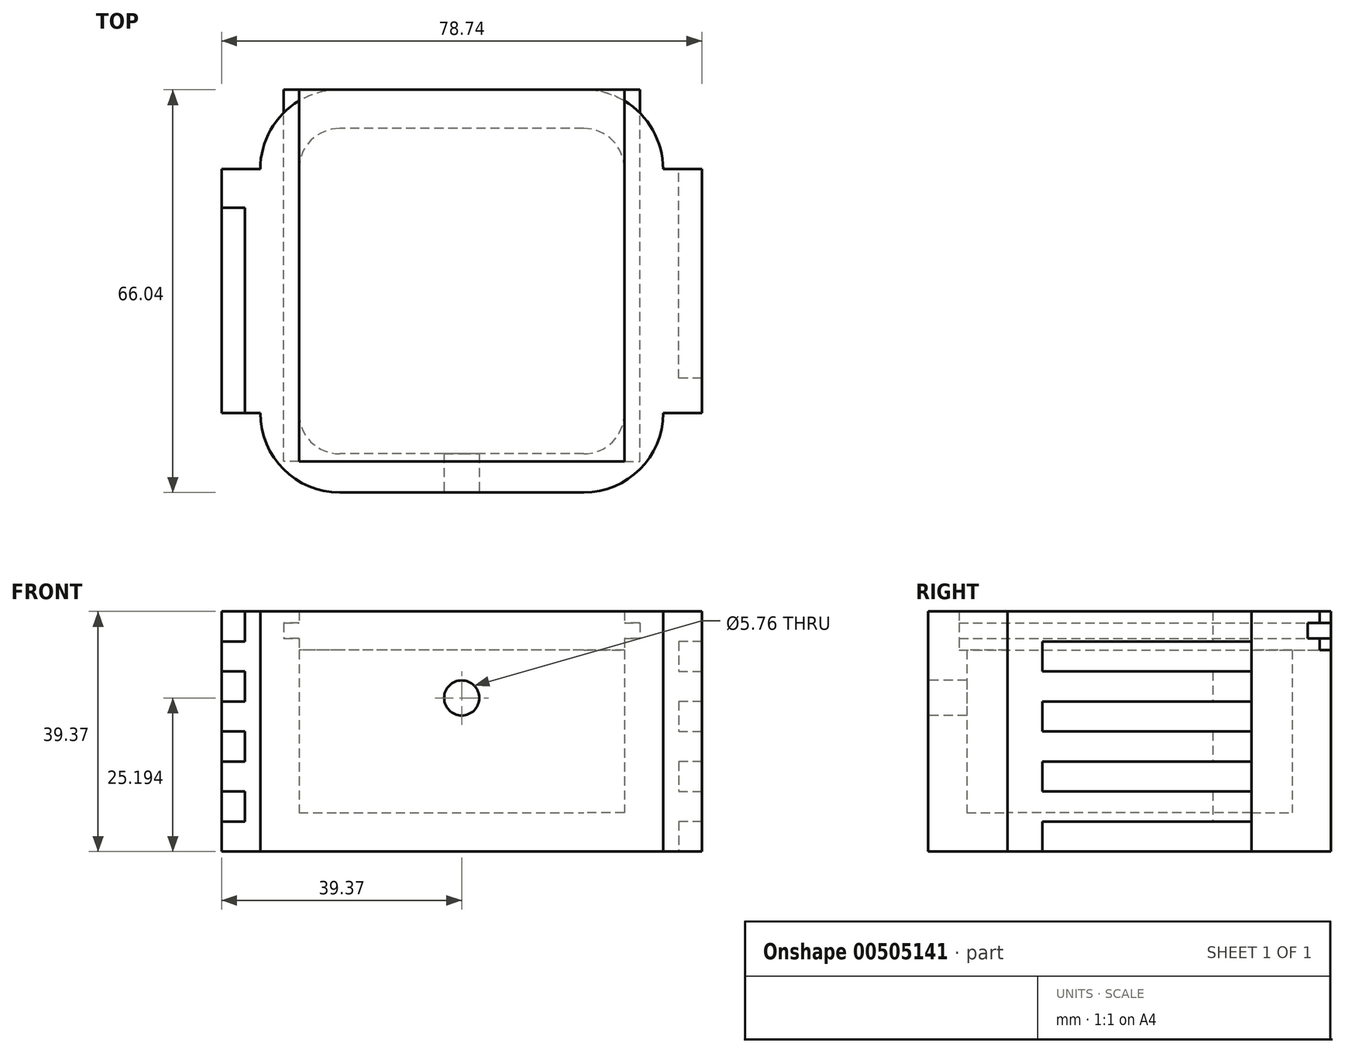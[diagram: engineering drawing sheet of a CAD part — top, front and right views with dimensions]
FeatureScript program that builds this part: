
annotation { "Feature Type Name" : "Feature", "Feature Type Description" : "" }
export const myFeature = defineFeature(function(context is Context, id is Id, definition is map)
    precondition{}
    {
        {
            var Q0;
            Q0=qCreatedBy(makeId("Top.planeOp"),FACE);
            var sketch = newSketch(context, id + "F0", { "sketchPlane" : qUnion([Q0])});
            skLineSegment(sketch, "E0", {"start": v(-20, 26.67) * mm, "end": v(20, 26.67) * mm});
            skLineSegment(sketch, "E1.MirrorCS", {"start": v(-20, -26.67) * mm, "end": v(20, -26.67) * mm});
            skLineSegment(sketch, "E2", {"start": v(-26.67, 20) * mm, "end": v(-26.67, -20) * mm});
            skLineSegment(sketch, "E3.MirrorCS", {"start": v(26.67, 20) * mm, "end": v(26.67, -20) * mm});
            skPoint(sketch, "E4.visualSharp", {"position": v(-26.67, 26.67) * mm});
            skArc(sketch, "E4.filletArc", {"start": v(-20, 26.67) * mm, "mid": v(-24.72, 24.72) * mm, "end": v(-26.67, 20) * mm});
            skPoint(sketch, "E5.visualSharp", {"position": v(26.67, 26.67) * mm});
            skArc(sketch, "E5.filletArc", {"start": v(26.67, 20) * mm, "mid": v(24.72, 24.72) * mm, "end": v(20, 26.67) * mm});
            skPoint(sketch, "E6.visualSharp", {"position": v(26.67, -26.67) * mm});
            skArc(sketch, "E6.filletArc", {"start": v(20, -26.67) * mm, "mid": v(24.72, -24.72) * mm, "end": v(26.67, -20) * mm});
            skPoint(sketch, "E7.visualSharp", {"position": v(-26.67, -26.67) * mm});
            skArc(sketch, "E7.filletArc", {"start": v(-26.67, -20) * mm, "mid": v(-24.72, -24.72) * mm, "end": v(-20, -26.67) * mm});
            skPoint(sketch, "E8", {"position": v(0, 33.02) * mm});
            skLineSegment(sketch, "E9", {"start": v(-20, 33.02) * mm, "end": v(20, 33.02) * mm});
            skLineSegment(sketch, "E10.MirrorCS", {"start": v(-20, -33.02) * mm, "end": v(20, -33.02) * mm});
            skPoint(sketch, "E11", {"position": v(33.02, 0) * mm});
            skPoint(sketch, "E11.positionSnap0", {"position": v(26.67, 0) * mm});
            skLineSegment(sketch, "E12", {"start": v(33.02, 20) * mm, "end": v(33.02, -20) * mm});
            skLineSegment(sketch, "E13.MirrorCS", {"start": v(-33.02, 20) * mm, "end": v(-33.02, -20) * mm});
            skArc(sketch, "E14", {"start": v(33.02, 20) * mm, "mid": v(29.2, 29.2) * mm, "end": v(20, 33.02) * mm});
            skArc(sketch, "E15.MirrorCS", {"start": v(-33.02, 20) * mm, "mid": v(-29.2, 29.2) * mm, "end": v(-20, 33.02) * mm});
            skArc(sketch, "E16.MirrorCS", {"start": v(-33.02, -20) * mm, "mid": v(-29.2, -29.2) * mm, "end": v(-20, -33.02) * mm});
            skArc(sketch, "E17.MirrorCS", {"start": v(33.02, -20) * mm, "mid": v(29.2, -29.2) * mm, "end": v(20, -33.02) * mm});
            skSolve(sketch);
        }
        {
            var Q0;
            Q0 = qSketchRegion(id + "F0", true);
            extrude(context, id + "F1", {"entities" : qUnion([Q0]), "depth" : 39.37 * mm});
        }
        {
            var Q0;
            Q0=makeQuery(id+"F0.imprint","IMPRINT",FACE,{"disambiguationData":[TD([[makeQuery(id+"F0.imprint","IMPRINT",EDGE,{"derivedFrom":sQuery(id+"F0.wireOp",EDGE,"E0")}),-1.0]])]});
            extrude(context, id + "F2", {"entities" : qUnion([Q0]), "operationType" : NewBodyOperationType.ADD, "depth" : 6.35 * mm});
        }
        {
            var Q0;
            Q0=makeQuery(id+"F1.opExtrude","SWEPT_FACE",FACE,{"disambiguationData":[OSD([sQuery(id+"F0.wireOp",EDGE,"E9")])]});
            var sketch = newSketch(context, id + "F3", { "sketchPlane" : qUnion([Q0])});
            skPoint(sketch, "E18", {"position": v(0, 39.37) * mm});
            skPoint(sketch, "E19", {"position": v(20, 29.99) * mm});
            skPoint(sketch, "E20", {"position": v(33, 29.99) * mm});
            skPoint(sketch, "E21.MirrorP", {"position": v(-20, 29.99) * mm});
            skPoint(sketch, "E22.MirrorP", {"position": v(-26.66, 29.99) * mm});
            skPoint(sketch, "E23.MirrorP", {"position": v(-33, 29.99) * mm});
            skLineSegment(sketch, "E24", {"start": v(0, 39.37) * mm, "end": v(26.67, 39.37) * mm});
            skLineSegment(sketch, "E25.MirrorCS", {"start": v(0, 39.37) * mm, "end": v(-26.67, 39.37) * mm});
            skPoint(sketch, "E26", {"position": v(0, 0) * mm});
            skPoint(sketch, "E27", {"position": v(0, 6.35) * mm});
            skPoint(sketch, "E28", {"position": v(-26.67, 33.02) * mm});
            skPoint(sketch, "E29", {"position": v(-26.67, 39.37) * mm});
            skPoint(sketch, "E30.MirrorP", {"position": v(26.67, 33.02) * mm});
            skLineSegment(sketch, "E31", {"start": v(-26.67, 33.02) * mm, "end": v(26.67, 33.02) * mm});
            skLineSegment(sketch, "E32", {"start": v(26.67, 39.37) * mm, "end": v(26.67, 33.02) * mm});
            skLineSegment(sketch, "E33", {"start": v(-26.67, 39.37) * mm, "end": v(-26.67, 33.02) * mm});
            skPoint(sketch, "E34", {"position": v(-26.67, 37.46) * mm});
            skPoint(sketch, "E35", {"position": v(-26.67, 34.92) * mm});
            skPoint(sketch, "E36", {"position": v(-29.2, 34.92) * mm});
            skPoint(sketch, "E37", {"position": v(-29.2, 37.46) * mm});
            skLineSegment(sketch, "E38", {"start": v(-26.67, 37.46) * mm, "end": v(-29.2, 37.46) * mm});
            skLineSegment(sketch, "E39", {"start": v(-29.2, 34.92) * mm, "end": v(-26.67, 34.92) * mm});
            skLineSegment(sketch, "E40.MirrorCS", {"start": v(26.67, 37.46) * mm, "end": v(29.2, 37.46) * mm});
            skLineSegment(sketch, "E41.MirrorCS", {"start": v(29.2, 34.92) * mm, "end": v(26.67, 34.92) * mm});
            skLineSegment(sketch, "E42", {"start": v(-29.2, 37.46) * mm, "end": v(-29.2, 34.92) * mm});
            skLineSegment(sketch, "E43.MirrorCS", {"start": v(29.2, 37.46) * mm, "end": v(29.2, 34.92) * mm});
            skSolve(sketch);
        }
        {
            var Q0;
            {var subQ0=sQuery(id+"F3.wireOp",EDGE,"E38");Q0=makeQuery(id+"F3.imprint","IMPRINT",FACE,{"disambiguationData":[TD([[makeQuery(id+"F3.imprint","IMPRINT",EDGE,{"derivedFrom":subQ0}),1.0]])]});}
            var Q1;
            {var subQ0=sQuery(id+"F3.wireOp",EDGE,"E40.MirrorCS");Q1=makeQuery(id+"F3.imprint","IMPRINT",FACE,{"disambiguationData":[TD([[makeQuery(id+"F3.imprint","IMPRINT",EDGE,{"derivedFrom":subQ0}),-1.0]])]});}
            var Q2;
            {var subQ0=sQuery(id+"F3.wireOp",EDGE,"E24");var subQ6=sQuery(id+"F3.wireOp",EDGE,"E25.MirrorCS");var subQ9=makeQuery(id+"F3.imprint","INTERSECT",VERTEX,{"derivedFrom":[subQ0,subQ6]});Q2=makeQuery(id+"F3.imprint","IMPRINT",FACE,{"disambiguationData":[TD([[makeQuery(id+"F3.imprint","IMPRINT",EDGE,{"disambiguationData":[TD([[subQ9,1.0]])],"derivedFrom":subQ0}),1.0]])]});}
            var Q3;
            {var subQ0=sQuery(id+"F3.wireOp",EDGE,"E33");var subQ3=sQuery(id+"F3.wireOp",EDGE,"E25.MirrorCS");var subQ4=makeQuery(id+"F3.imprint","INTERSECT",VERTEX,{"derivedFrom":[subQ3,subQ0]});Q3=makeQuery(id+"F3.imprint","IMPRINT",FACE,{"disambiguationData":[TD([[makeQuery(id+"F3.imprint","IMPRINT",EDGE,{"disambiguationData":[TD([[subQ4,-1.0]])],"derivedFrom":subQ0}),1.0]])]});}
            var Q4;
            {var subQ0=sQuery(id+"F3.wireOp",EDGE,"E32");var subQ3=sQuery(id+"F3.wireOp",EDGE,"E24");var subQ4=makeQuery(id+"F3.imprint","INTERSECT",VERTEX,{"derivedFrom":[subQ3,subQ0]});Q4=makeQuery(id+"F3.imprint","IMPRINT",FACE,{"disambiguationData":[TD([[makeQuery(id+"F3.imprint","IMPRINT",EDGE,{"disambiguationData":[TD([[subQ4,-1.0]])],"derivedFrom":subQ0}),-1.0]])]});}
            extrude(context, id + "F4", {"entities" : qUnion([Q0, Q1, Q2, Q3, Q4]), "operationType" : NewBodyOperationType.REMOVE, "oppositeDirection" : true, "depth" : 60.96 * mm});
        }
        {
            var Q0;
            {var subQ0=sQuery(id+"F3.wireOp",EDGE,"E40.MirrorCS");Q0=makeQuery(id+"F3.imprint","IMPRINT",FACE,{"disambiguationData":[TD([[makeQuery(id+"F3.imprint","IMPRINT",EDGE,{"derivedFrom":subQ0}),-1.0]])]});}
            var Q1;
            {var subQ0=sQuery(id+"F3.wireOp",EDGE,"E24");var subQ6=sQuery(id+"F3.wireOp",EDGE,"E25.MirrorCS");var subQ9=makeQuery(id+"F3.imprint","INTERSECT",VERTEX,{"derivedFrom":[subQ0,subQ6]});Q1=makeQuery(id+"F3.imprint","IMPRINT",FACE,{"disambiguationData":[TD([[makeQuery(id+"F3.imprint","IMPRINT",EDGE,{"disambiguationData":[TD([[subQ9,1.0]])],"derivedFrom":subQ0}),1.0]])]});}
            var Q2;
            {var subQ0=sQuery(id+"F3.wireOp",EDGE,"E32");var subQ3=sQuery(id+"F3.wireOp",EDGE,"E24");var subQ4=makeQuery(id+"F3.imprint","INTERSECT",VERTEX,{"derivedFrom":[subQ3,subQ0]});Q2=makeQuery(id+"F3.imprint","IMPRINT",FACE,{"disambiguationData":[TD([[makeQuery(id+"F3.imprint","IMPRINT",EDGE,{"disambiguationData":[TD([[subQ4,-1.0]])],"derivedFrom":subQ0}),-1.0]])]});}
            var Q3;
            {var subQ0=sQuery(id+"F3.wireOp",EDGE,"E33");var subQ3=sQuery(id+"F3.wireOp",EDGE,"E25.MirrorCS");var subQ4=makeQuery(id+"F3.imprint","INTERSECT",VERTEX,{"derivedFrom":[subQ3,subQ0]});Q3=makeQuery(id+"F3.imprint","IMPRINT",FACE,{"disambiguationData":[TD([[makeQuery(id+"F3.imprint","IMPRINT",EDGE,{"disambiguationData":[TD([[subQ4,-1.0]])],"derivedFrom":subQ0}),1.0]])]});}
            var Q4;
            {var subQ0=sQuery(id+"F3.wireOp",EDGE,"E38");Q4=makeQuery(id+"F3.imprint","IMPRINT",FACE,{"disambiguationData":[TD([[makeQuery(id+"F3.imprint","IMPRINT",EDGE,{"derivedFrom":subQ0}),1.0]])]});}
            extrude(context, id + "F5", {"entities" : qUnion([Q0, Q1, Q2, Q3, Q4]), "oppositeDirection" : true, "depth" : 60.96 * mm});
        }
        {
            var Q0;
            Q0=makeQuery(id+"F1.opExtrude","SWEPT_FACE",FACE,{"disambiguationData":[OSD([sQuery(id+"F0.wireOp",EDGE,"E12")])]});
            var sketch = newSketch(context, id + "F6", { "sketchPlane" : qUnion([Q0])});
            skLineSegment(sketch, "E44.bottom", {"start": v(20, 39.37) * mm, "end": v(-20, 39.37) * mm});
            skLineSegment(sketch, "E44.top", {"start": v(20, 0) * mm, "end": v(-20, 0) * mm});
            skLineSegment(sketch, "E44.left", {"start": v(20, 39.37) * mm, "end": v(20, 0) * mm});
            skLineSegment(sketch, "E44.right", {"start": v(-20, 39.37) * mm, "end": v(-20, 0) * mm});
            skSolve(sketch);
        }
        {
            var Q0;
            Q0 = qSketchRegion(id + "F6", true);
            extrude(context, id + "F7", {"entities" : qUnion([Q0]), "operationType" : NewBodyOperationType.ADD, "depth" : 6.35 * mm});
        }
        {
            var Q0;
            Q0=makeQuery(id+"F7.opExtrude","SWEPT_FACE",FACE,{"disambiguationData":[OSD([sQuery(id+"F6.wireOp",EDGE,"E44.left")])]});
            var sketch = newSketch(context, id + "F8", { "sketchPlane" : qUnion([Q0])});
            skPoint(sketch, "E45", {"position": v(-39.37, 19.69) * mm});
            skPoint(sketch, "E46", {"position": v(-39.37, 39.37) * mm});
            skPoint(sketch, "E47", {"position": v(-39.37, 0) * mm});
            skPoint(sketch, "E48", {"position": v(-39.37, 29.53) * mm});
            skPoint(sketch, "E49.MirrorP", {"position": v(-39.37, 9.84) * mm});
            skPoint(sketch, "E50", {"position": v(-39.37, 34.44) * mm});
            skPoint(sketch, "E51.MirrorP", {"position": v(-39.37, 24.61) * mm});
            skPoint(sketch, "E52.MirrorP", {"position": v(-39.37, 14.76) * mm});
            skPoint(sketch, "E53.MirrorP", {"position": v(-39.37, 4.93) * mm});
            skLineSegment(sketch, "E54", {"start": v(39.37, 4.93) * mm, "end": v(35.56, 4.93) * mm});
            skLineSegment(sketch, "E55", {"start": v(35.56, 4.93) * mm, "end": v(35.56, 9.84) * mm});
            skLineSegment(sketch, "E56", {"start": v(35.56, 9.84) * mm, "end": v(39.37, 9.84) * mm});
            skLineSegment(sketch, "E57", {"start": v(39.37, 14.76) * mm, "end": v(35.56, 14.76) * mm});
            skLineSegment(sketch, "E58", {"start": v(35.56, 14.76) * mm, "end": v(35.56, 19.68) * mm});
            skLineSegment(sketch, "E59", {"start": v(35.56, 19.68) * mm, "end": v(39.37, 19.68) * mm});
            skLineSegment(sketch, "E60", {"start": v(39.37, 24.61) * mm, "end": v(35.56, 24.61) * mm});
            skLineSegment(sketch, "E61", {"start": v(35.56, 24.61) * mm, "end": v(35.56, 29.53) * mm});
            skLineSegment(sketch, "E62", {"start": v(35.56, 29.53) * mm, "end": v(39.37, 29.53) * mm});
            skLineSegment(sketch, "E63", {"start": v(39.37, 34.44) * mm, "end": v(35.56, 34.44) * mm});
            skLineSegment(sketch, "E64", {"start": v(35.56, 34.44) * mm, "end": v(35.56, 39.37) * mm});
            skLineSegment(sketch, "E65", {"start": v(-35.56, 0) * mm, "end": v(-39.37, 0) * mm});
            skPoint(sketch, "E66", {"position": v(0, 20.46) * mm});
            skPoint(sketch, "E67", {"position": v(0, 39.45) * mm});
            skLineSegment(sketch, "E68", {"start": v(39.37, 0) * mm, "end": v(39.37, 4.93) * mm});
            skLineSegment(sketch, "E69", {"start": v(39.37, 0) * mm, "end": v(33.02, 0) * mm});
            skLineSegment(sketch, "E70", {"start": v(33.02, 0) * mm, "end": v(33.02, 39.37) * mm});
            skLineSegment(sketch, "E71", {"start": v(33.02, 39.37) * mm, "end": v(35.56, 39.37) * mm});
            skLineSegment(sketch, "E72", {"start": v(39.37, 14.76) * mm, "end": v(39.37, 9.84) * mm});
            skLineSegment(sketch, "E73", {"start": v(39.37, 34.44) * mm, "end": v(39.37, 29.53) * mm});
            skLineSegment(sketch, "E74", {"start": v(39.37, 24.61) * mm, "end": v(39.37, 19.68) * mm});
            skLineSegment(sketch, "E75", {"start": v(-39.37, 34.44) * mm, "end": v(-35.56, 34.44) * mm});
            skLineSegment(sketch, "E76", {"start": v(-35.56, 34.44) * mm, "end": v(-35.56, 29.53) * mm});
            skLineSegment(sketch, "E77", {"start": v(-35.56, 29.53) * mm, "end": v(-39.37, 29.53) * mm});
            skLineSegment(sketch, "E78", {"start": v(-39.37, 24.61) * mm, "end": v(-35.56, 24.61) * mm});
            skLineSegment(sketch, "E79", {"start": v(-35.56, 24.61) * mm, "end": v(-35.56, 19.69) * mm});
            skLineSegment(sketch, "E80", {"start": v(-35.56, 19.69) * mm, "end": v(-39.37, 19.69) * mm});
            skLineSegment(sketch, "E81", {"start": v(-39.37, 14.76) * mm, "end": v(-35.56, 14.76) * mm});
            skLineSegment(sketch, "E82", {"start": v(-35.56, 14.76) * mm, "end": v(-35.56, 9.84) * mm});
            skLineSegment(sketch, "E83", {"start": v(-35.56, 9.84) * mm, "end": v(-39.37, 9.84) * mm});
            skLineSegment(sketch, "E84", {"start": v(-39.37, 4.93) * mm, "end": v(-35.56, 4.93) * mm});
            skLineSegment(sketch, "E85", {"start": v(-35.56, 4.93) * mm, "end": v(-35.56, 0) * mm});
            skLineSegment(sketch, "E86", {"start": v(-39.37, 39.37) * mm, "end": v(-39.37, 34.44) * mm});
            skLineSegment(sketch, "E87", {"start": v(-39.37, 39.37) * mm, "end": v(-33.02, 39.37) * mm});
            skLineSegment(sketch, "E88", {"start": v(-33.02, 39.37) * mm, "end": v(-33.02, 0) * mm});
            skLineSegment(sketch, "E89", {"start": v(-33.02, 0) * mm, "end": v(-35.56, 0) * mm});
            skLineSegment(sketch, "E90", {"start": v(-39.37, 24.61) * mm, "end": v(-39.37, 29.53) * mm});
            skLineSegment(sketch, "E91", {"start": v(-39.37, 4.93) * mm, "end": v(-39.37, 9.84) * mm});
            skLineSegment(sketch, "E92", {"start": v(-39.37, 14.76) * mm, "end": v(-39.37, 19.69) * mm});
            skLineSegment(sketch, "E93", {"start": v(35.56, 39.37) * mm, "end": v(39.37, 39.37) * mm});
            skLineSegment(sketch, "E94", {"start": v(39.37, 39.37) * mm, "end": v(39.37, 34.44) * mm});
            skLineSegment(sketch, "E95", {"start": v(39.37, 29.53) * mm, "end": v(39.37, 24.61) * mm});
            skLineSegment(sketch, "E96", {"start": v(39.37, 19.68) * mm, "end": v(39.37, 14.76) * mm});
            skLineSegment(sketch, "E97", {"start": v(39.37, 9.84) * mm, "end": v(39.37, 4.93) * mm});
            skSolve(sketch);
        }
        {
            var Q0;
            Q0=makeQuery(id+"F1.opExtrude","SWEPT_FACE",FACE,{"disambiguationData":[OSD([sQuery(id+"F0.wireOp",EDGE,"E13.MirrorCS")])]});
            extrude(context, id + "F9", {"entities" : qUnion([Q0]), "operationType" : NewBodyOperationType.ADD, "depth" : 6.35 * mm});
        }
        {
            var Q0;
            {var subQ0=sQuery(id+"F8.wireOp",EDGE,"E75");Q0=makeQuery(id+"F8.imprint","IMPRINT",FACE,{"disambiguationData":[TD([[makeQuery(id+"F8.imprint","IMPRINT",EDGE,{"derivedFrom":subQ0}),-1.0]])]});}
            var Q1;
            {var subQ0=sQuery(id+"F8.wireOp",EDGE,"E78");Q1=makeQuery(id+"F8.imprint","IMPRINT",FACE,{"disambiguationData":[TD([[makeQuery(id+"F8.imprint","IMPRINT",EDGE,{"derivedFrom":subQ0}),-1.0]])]});}
            var Q2;
            {var subQ0=sQuery(id+"F8.wireOp",EDGE,"E81");Q2=makeQuery(id+"F8.imprint","IMPRINT",FACE,{"disambiguationData":[TD([[makeQuery(id+"F8.imprint","IMPRINT",EDGE,{"derivedFrom":subQ0}),-1.0]])]});}
            var Q3;
            {var subQ0=sQuery(id+"F8.wireOp",EDGE,"E65");Q3=makeQuery(id+"F8.imprint","IMPRINT",FACE,{"disambiguationData":[TD([[makeQuery(id+"F8.imprint","IMPRINT",EDGE,{"derivedFrom":subQ0}),1.0]])]});}
            extrude(context, id + "F10", {"entities" : qUnion([Q0, Q1, Q2, Q3]), "operationType" : NewBodyOperationType.REMOVE, "oppositeDirection" : true, "depth" : 34.3 * mm});
        }
        {
            var Q0;
            Q0=makeQuery(id+"F8.imprint","IMPRINT",FACE,{"disambiguationData":[TD([[makeQuery(id+"F8.imprint","IMPRINT",EDGE,{"derivedFrom":sQuery(id+"F8.wireOp",EDGE,"E63")}),-1.0]])]});
            var Q1;
            Q1=makeQuery(id+"F8.imprint","IMPRINT",FACE,{"disambiguationData":[TD([[makeQuery(id+"F8.imprint","IMPRINT",EDGE,{"derivedFrom":sQuery(id+"F8.wireOp",EDGE,"E60")}),-1.0]])]});
            var Q2;
            Q2=makeQuery(id+"F8.imprint","IMPRINT",FACE,{"disambiguationData":[TD([[makeQuery(id+"F8.imprint","IMPRINT",EDGE,{"derivedFrom":sQuery(id+"F8.wireOp",EDGE,"E57")}),-1.0]])]});
            var Q3;
            Q3=makeQuery(id+"F8.imprint","IMPRINT",FACE,{"disambiguationData":[TD([[makeQuery(id+"F8.imprint","IMPRINT",EDGE,{"derivedFrom":sQuery(id+"F8.wireOp",EDGE,"E54")}),-1.0]])]});
            extrude(context, id + "F11", {"entities" : qUnion([Q0, Q1, Q2, Q3]), "operationType" : NewBodyOperationType.REMOVE, "oppositeDirection" : true, "depth" : 47.5 * mm, "hasSecondDirection" : true, "secondDirectionOppositeDirection" : true, "secondDirectionDepth" : 6.35 * mm});
        }
        {
            var Q0;
            Q0=makeQuery(id+"F1.opExtrude","SWEPT_FACE",FACE,{"disambiguationData":[OSD([sQuery(id+"F0.wireOp",EDGE,"E10.MirrorCS")])]});
            var sketch = newSketch(context, id + "F12", { "sketchPlane" : qUnion([Q0])});
            skCircle(sketch, "E98", {"center": v(0, 25.2) * mm, "radius": 2.88 * mm});
            skSolve(sketch);
        }
        {
            var Q0;
            Q0 = qSketchRegion(id + "F12", true);
            extrude(context, id + "F13", {"entities" : qUnion([Q0]), "operationType" : NewBodyOperationType.REMOVE, "oppositeDirection" : true, "depth" : 8.9 * mm});
        }
    });
